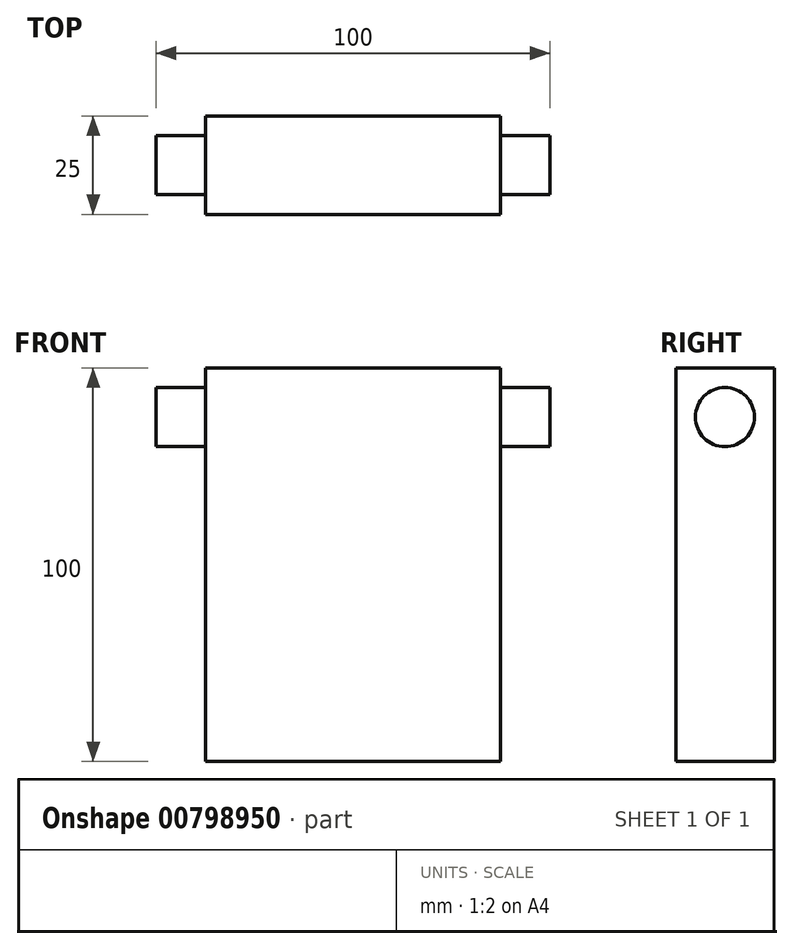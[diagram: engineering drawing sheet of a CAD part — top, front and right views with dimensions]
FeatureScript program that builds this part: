
annotation { "Feature Type Name" : "Feature", "Feature Type Description" : "" }
export const myFeature = defineFeature(function(context is Context, id is Id, definition is map)
    precondition{}
    {
        {
            var Q0;
            Q0=qCreatedBy(makeId("Front.planeOp"),FACE);
            var sketch = newSketch(context, id + "F0", { "sketchPlane" : qUnion([Q0])});
            skLineSegment(sketch, "E0.bottom", {"start": v(-37.5, -50) * mm, "end": v(37.5, -50) * mm});
            skLineSegment(sketch, "E0.top", {"start": v(-37.5, 50) * mm, "end": v(37.5, 50) * mm});
            skLineSegment(sketch, "E0.left", {"start": v(-37.5, -50) * mm, "end": v(-37.5, 50) * mm});
            skLineSegment(sketch, "E0.right", {"start": v(37.5, -50) * mm, "end": v(37.5, 50) * mm});
            skPoint(sketch, "E0.middle", {"position": v(0, 0) * mm});
            skSolve(sketch);
        }
        {
            var Q0;
            Q0=makeQuery(id+"F0.imprint","IMPRINT",FACE,{"disambiguationData":[TD([[makeQuery(id+"F0.imprint","IMPRINT",EDGE,{"derivedFrom":sQuery(id+"F0.wireOp",EDGE,"E0.bottom")}),1.0]])]});
            extrude(context, id + "F1", {"entities" : qUnion([Q0]), "endBound" : BoundingType.SYMMETRIC, "depth" : 25 * mm, "offsetDistance" : 25 * mm});
        }
        {
            var Q0;
            Q0=qCreatedBy(makeId("Right.planeOp"),FACE);
            var sketch = newSketch(context, id + "F2", { "sketchPlane" : qUnion([Q0])});
            skCircle(sketch, "E1", {"center": v(0, 37.5) * mm, "radius": 7.5 * mm});
            skSolve(sketch);
        }
        {
            var Q0;
            Q0=makeQuery(id+"F2.imprint","IMPRINT",FACE,{"disambiguationData":[TD([[makeQuery(id+"F2.imprint","IMPRINT",EDGE,{"derivedFrom":sQuery(id+"F2.wireOp",EDGE,"E1")}),1.0]])]});
            extrude(context, id + "F3", {"entities" : qUnion([Q0]), "operationType" : NewBodyOperationType.ADD, "endBound" : BoundingType.SYMMETRIC, "depth" : 100 * mm, "offsetDistance" : 25 * mm});
        }
    });
